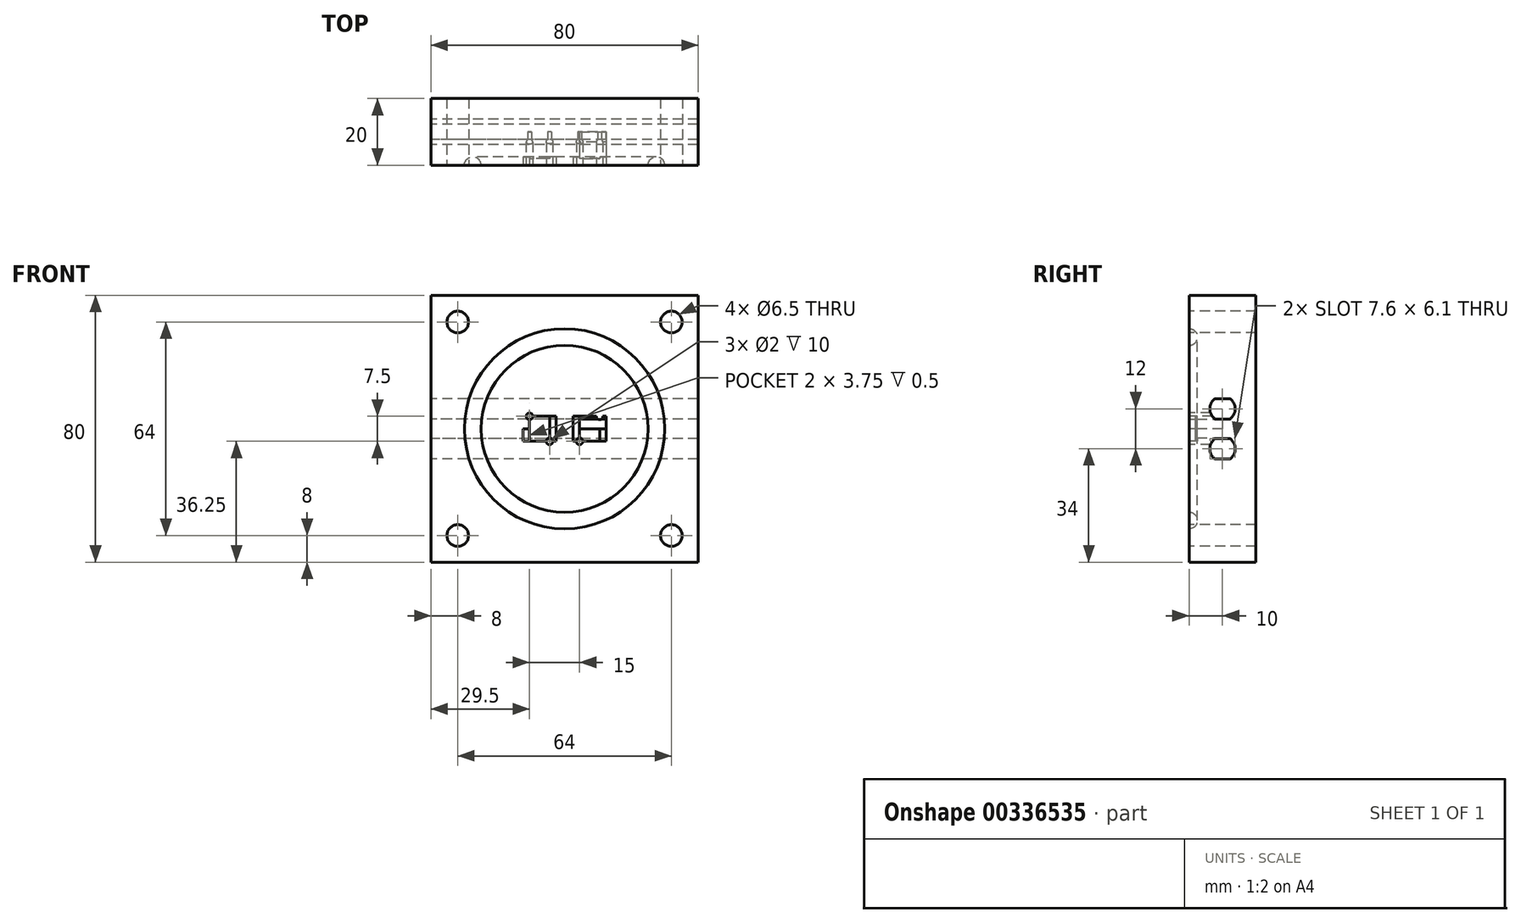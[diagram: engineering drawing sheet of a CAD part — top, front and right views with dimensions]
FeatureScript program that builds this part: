
annotation { "Feature Type Name" : "Feature", "Feature Type Description" : "" }
export const myFeature = defineFeature(function(context is Context, id is Id, definition is map)
    precondition{}
    {
        {
            assignVariable(context, id + "F0", {"name" : "Thickness", "anyValue" : 20});
        }
        {
            var Q0;
            Q0=qCreatedBy(makeId("Front.planeOp"),FACE);
            var sketch = newSketch(context, id + "F1", { "sketchPlane" : qUnion([Q0])});
            skLineSegment(sketch, "E0.bottom", {"start": v(0, 0) * mm, "end": v(80, 0) * mm});
            skLineSegment(sketch, "E0.top", {"start": v(0, 80) * mm, "end": v(80, 80) * mm});
            skLineSegment(sketch, "E0.left", {"start": v(0, 0) * mm, "end": v(0, 80) * mm});
            skLineSegment(sketch, "E0.right", {"start": v(80, 0) * mm, "end": v(80, 80) * mm});
            skSolve(sketch);
        }
        {
            var Q0;
            Q0=makeQuery(id+"F1.imprint","IMPRINT",FACE,{"disambiguationData":[TD([[makeQuery(id+"F1.imprint","IMPRINT",EDGE,{"derivedFrom":sQuery(id+"F1.wireOp",EDGE,"E0.bottom")}),1.0]])]});
            extrude(context, id + "F2", {"entities" : qUnion([Q0]), "depth" : (getVariable(context, 'Thickness')) * mm});
        }
        {
            assignVariable(context, id + "F3", {"name" : "G_thick", "anyValue" : 5});
        }
        {
            var Q0;
            Q0=makeQuery(id+"F2.opExtrude","CAP_FACE",FACE,{"disambiguationData":[OSD([sQuery(id+"F1.wireOp",EDGE,"E0.bottom"),sQuery(id+"F1.wireOp",EDGE,"E0.top"),sQuery(id+"F1.wireOp",EDGE,"E0.left"),sQuery(id+"F1.wireOp",EDGE,"E0.right")])],"isStart":false});
            var sketch = newSketch(context, id + "F4", { "sketchPlane" : qUnion([Q0])});
            skCircle(sketch, "E1", {"center": v(40, 40) * mm, "radius": 30 * mm});
            skCircle(sketch, "E2", {"center": v(40, 40) * mm, "radius": 25 * mm});
            skCircle(sketch, "E3", {"center": v(8, 72) * mm, "radius": 3.25 * mm});
            skCircle(sketch, "E4", {"center": v(8, 8) * mm, "radius": 3.25 * mm});
            skCircle(sketch, "E5", {"center": v(72, 8) * mm, "radius": 3.25 * mm});
            skCircle(sketch, "E6", {"center": v(72, 72) * mm, "radius": 3.25 * mm});
            skLineSegment(sketch, "E7.bottom", {"start": v(27.5, 45) * mm, "end": v(52.5, 45) * mm});
            skLineSegment(sketch, "E7.top", {"start": v(27.5, 35) * mm, "end": v(52.5, 35) * mm});
            skLineSegment(sketch, "E7.left", {"start": v(27.5, 45) * mm, "end": v(27.5, 35) * mm});
            skLineSegment(sketch, "E7.right", {"start": v(52.5, 45) * mm, "end": v(52.5, 35) * mm});
            skLineSegment(sketch, "E8", {"start": v(27.5, 40) * mm, "end": v(52.5, 40) * mm});
            skLineSegment(sketch, "E9.bottom", {"start": v(37.5, 36.25) * mm, "end": v(27.5, 36.25) * mm});
            skLineSegment(sketch, "E9.top", {"start": v(37.5, 43.75) * mm, "end": v(27.5, 43.75) * mm});
            skLineSegment(sketch, "E9.left", {"start": v(37.5, 36.25) * mm, "end": v(37.5, 43.75) * mm});
            skLineSegment(sketch, "E9.right", {"start": v(27.5, 36.25) * mm, "end": v(27.5, 43.75) * mm});
            skPoint(sketch, "E9.middle", {"position": v(32.5, 40) * mm});
            skLineSegment(sketch, "E10", {"start": v(40, 45) * mm, "end": v(40, 33.09) * mm});
            skPoint(sketch, "E10.endSnap0", {"position": v(40, 35) * mm});
            skLineSegment(sketch, "E11", {"start": v(40, 33.09) * mm, "end": v(40, 48.3) * mm, "construction": true});
            skLineSegment(sketch, "E12.MirrorCS", {"start": v(42.5, 43.75) * mm, "end": v(52.5, 43.75) * mm});
            skLineSegment(sketch, "E13.MirrorCS", {"start": v(42.5, 36.25) * mm, "end": v(42.5, 43.75) * mm});
            skLineSegment(sketch, "E14.MirrorCS", {"start": v(42.5, 36.25) * mm, "end": v(52.5, 36.25) * mm});
            skLineSegment(sketch, "E15.MirrorCS", {"start": v(52.5, 36.25) * mm, "end": v(52.5, 43.75) * mm});
            skLineSegment(sketch, "E16.bottom", {"start": v(37.5, 36.25) * mm, "end": v(35.5, 36.25) * mm});
            skLineSegment(sketch, "E16.top", {"start": v(37.5, 43.75) * mm, "end": v(35.5, 43.75) * mm});
            skLineSegment(sketch, "E16.right", {"start": v(35.5, 36.25) * mm, "end": v(35.5, 43.75) * mm});
            skLineSegment(sketch, "E17.bottom", {"start": v(27.5, 36.25) * mm, "end": v(29.5, 36.25) * mm});
            skLineSegment(sketch, "E17.top", {"start": v(27.5, 43.75) * mm, "end": v(29.5, 43.75) * mm});
            skLineSegment(sketch, "E17.right", {"start": v(29.5, 36.25) * mm, "end": v(29.5, 43.75) * mm});
            skLineSegment(sketch, "E18.MirrorCS", {"start": v(44.5, 36.25) * mm, "end": v(44.5, 43.75) * mm});
            skLineSegment(sketch, "E19.MirrorCS", {"start": v(42.5, 36.25) * mm, "end": v(44.5, 36.25) * mm});
            skLineSegment(sketch, "E20.MirrorCS", {"start": v(50.5, 36.25) * mm, "end": v(50.5, 43.75) * mm});
            skLineSegment(sketch, "E21.MirrorCS", {"start": v(52.5, 43.75) * mm, "end": v(50.5, 43.75) * mm});
            skCircle(sketch, "E22", {"center": v(29.5, 43.75) * mm, "radius": 1 * mm});
            skCircle(sketch, "E23", {"center": v(35.5, 36.25) * mm, "radius": 1 * mm});
            skCircle(sketch, "E24.MirrorC", {"center": v(44.5, 36.25) * mm, "radius": 1 * mm});
            skCircle(sketch, "E25.MirrorC", {"center": v(50.5, 43.75) * mm, "radius": 1 * mm});
            skSolve(sketch);
        }
        {
            var Q0;
            Q0=makeQuery(id+"F4.imprint","IMPRINT",FACE,{"disambiguationData":[TD([[makeQuery(id+"F4.imprint","IMPRINT",EDGE,{"derivedFrom":sQuery(id+"F4.wireOp",EDGE,"E5")}),1.0]])]});
            var Q1;
            Q1=makeQuery(id+"F4.imprint","IMPRINT",FACE,{"disambiguationData":[TD([[makeQuery(id+"F4.imprint","IMPRINT",EDGE,{"derivedFrom":sQuery(id+"F4.wireOp",EDGE,"E4")}),1.0]])]});
            var Q2;
            Q2=makeQuery(id+"F4.imprint","IMPRINT",FACE,{"disambiguationData":[TD([[makeQuery(id+"F4.imprint","IMPRINT",EDGE,{"derivedFrom":sQuery(id+"F4.wireOp",EDGE,"E3")}),1.0]])]});
            var Q3;
            Q3=makeQuery(id+"F4.imprint","IMPRINT",FACE,{"disambiguationData":[TD([[makeQuery(id+"F4.imprint","IMPRINT",EDGE,{"derivedFrom":sQuery(id+"F4.wireOp",EDGE,"E6")}),1.0]])]});
            var Q4;
            Q4=sQuery(id+"F4.wireOp",EDGE,"E3");
            extrude(context, id + "F5", {"entities" : qUnion([Q0, Q1, Q2, Q3]), "operationType" : NewBodyOperationType.REMOVE, "surfaceEntities" : qUnion([Q4]), "endBound" : BoundingType.THROUGH_ALL, "oppositeDirection" : true, "depth" : 25 * mm});
        }
        {
            var Q0;
            Q0=makeQuery(id+"F4.imprint","IMPRINT",FACE,{"disambiguationData":[TD([[makeQuery(id+"F4.imprint","IMPRINT",EDGE,{"derivedFrom":sQuery(id+"F4.wireOp",EDGE,"E1")}),1.0]])]});
            var Q1;
            Q1=sQuery(id+"F4.wireOp",EDGE,"E1");
            var Q2;
            Q2=sQuery(id+"F4.wireOp",EDGE,"E2");
            extrude(context, id + "F6", {"entities" : qUnion([Q0]), "operationType" : NewBodyOperationType.REMOVE, "surfaceEntities" : qUnion([Q1, Q2]), "oppositeDirection" : true, "depth" : 2.5 * mm});
        }
        {
            var Q0;
            Q0=makeQuery(id+"F6.boolean.opBoolean","COPY",EDGE,{"derivedFrom":makeQuery(id+"F6.opExtrude","CAP_EDGE",EDGE,{"disambiguationData":[OSD([sQuery(id+"F4.wireOp",EDGE,"E2")])],"isStart":false})});
            fillet(context, id + "F7", {"entities" : qUnion([Q0]), "radius" : (getVariable(context, 'G_thick') / 2) * mm, "tangentPropagation" : true, "allowEdgeOverflow" : false});
        }
        {
            var Q0;
            Q0=makeQuery(id+"F6.boolean.opBoolean","COPY",EDGE,{"derivedFrom":makeQuery(id+"F6.opExtrude","CAP_EDGE",EDGE,{"disambiguationData":[OSD([sQuery(id+"F4.wireOp",EDGE,"E1")])],"isStart":false})});
            fillet(context, id + "F8", {"entities" : qUnion([Q0]), "radius" : (getVariable(context, 'G_thick') / 2) * mm, "tangentPropagation" : true, "allowEdgeOverflow" : false});
        }
        {
            var Q0;
            {var subQ5=sQuery(id+"F4.wireOp",EDGE,"E17.top");Q0=makeQuery(id+"F4.imprint","IMPRINT",FACE,{"disambiguationData":[TD([[makeQuery(id+"F4.imprint","IMPRINT",EDGE,{"derivedFrom":subQ5}),-1.0]])]});}
            var Q1;
            {var subQ5=sQuery(id+"F4.wireOp",EDGE,"E17.bottom");Q1=makeQuery(id+"F4.imprint","IMPRINT",FACE,{"disambiguationData":[TD([[makeQuery(id+"F4.imprint","IMPRINT",EDGE,{"derivedFrom":subQ5}),1.0]])]});}
            var Q2;
            {var subQ5=sQuery(id+"F4.wireOp",EDGE,"E16.top");Q2=makeQuery(id+"F4.imprint","IMPRINT",FACE,{"disambiguationData":[TD([[makeQuery(id+"F4.imprint","IMPRINT",EDGE,{"derivedFrom":subQ5}),1.0]])]});}
            var Q3;
            {var subQ5=sQuery(id+"F4.wireOp",EDGE,"E16.bottom");Q3=makeQuery(id+"F4.imprint","IMPRINT",FACE,{"disambiguationData":[TD([[makeQuery(id+"F4.imprint","IMPRINT",EDGE,{"derivedFrom":subQ5}),-1.0]])]});}
            var Q4;
            {var subQ0=sQuery(id+"F4.wireOp",EDGE,"E13.MirrorCS");var subQ1=sQuery(id+"F4.wireOp",EDGE,"E8");var subQ2=makeQuery(id+"F4.imprint","INTERSECT",VERTEX,{"derivedFrom":[subQ1,subQ0]});Q4=makeQuery(id+"F4.imprint","IMPRINT",FACE,{"disambiguationData":[TD([[makeQuery(id+"F4.imprint","IMPRINT",EDGE,{"disambiguationData":[TD([[subQ2,-1.0]])],"derivedFrom":subQ1}),1.0]])]});}
            var Q5;
            {var subQ0=sQuery(id+"F4.wireOp",EDGE,"E13.MirrorCS");var subQ1=sQuery(id+"F4.wireOp",EDGE,"E8");var subQ2=makeQuery(id+"F4.imprint","INTERSECT",VERTEX,{"derivedFrom":[subQ1,subQ0]});Q5=makeQuery(id+"F4.imprint","IMPRINT",FACE,{"disambiguationData":[TD([[makeQuery(id+"F4.imprint","IMPRINT",EDGE,{"disambiguationData":[TD([[subQ2,-1.0]])],"derivedFrom":subQ1}),-1.0]])]});}
            var Q6;
            {var subQ0=sQuery(id+"F4.wireOp",EDGE,"E15.MirrorCS");var subQ1=sQuery(id+"F4.wireOp",EDGE,"E8");var subQ2=makeQuery(id+"F4.imprint","INTERSECT",VERTEX,{"derivedFrom":[subQ1,subQ0]});Q6=makeQuery(id+"F4.imprint","IMPRINT",FACE,{"disambiguationData":[TD([[makeQuery(id+"F4.imprint","IMPRINT",EDGE,{"disambiguationData":[TD([[subQ2,1.0]])],"derivedFrom":subQ1}),-1.0]])]});}
            var Q7;
            {var subQ5=sQuery(id+"F4.wireOp",EDGE,"E21.MirrorCS");Q7=makeQuery(id+"F4.imprint","IMPRINT",FACE,{"disambiguationData":[TD([[makeQuery(id+"F4.imprint","IMPRINT",EDGE,{"derivedFrom":subQ5}),1.0]])]});}
            var Q8;
            {var subQ0=sQuery(id+"F4.wireOp",EDGE,"E9.right");var subQ1=sQuery(id+"F4.wireOp",EDGE,"E8");var subQ2=makeQuery(id+"F4.imprint","INTERSECT",VERTEX,{"derivedFrom":[subQ1,subQ0]});Q8=makeQuery(id+"F4.imprint","IMPRINT",FACE,{"disambiguationData":[TD([[makeQuery(id+"F4.imprint","IMPRINT",EDGE,{"disambiguationData":[TD([[subQ2,-1.0]])],"derivedFrom":subQ1}),1.0]])]});}
            var Q9;
            {var subQ0=sQuery(id+"F4.wireOp",EDGE,"E16.right");var subQ1=sQuery(id+"F4.wireOp",EDGE,"E8");var subQ2=makeQuery(id+"F4.imprint","INTERSECT",VERTEX,{"derivedFrom":[subQ1,subQ0]});Q9=makeQuery(id+"F4.imprint","IMPRINT",FACE,{"disambiguationData":[TD([[makeQuery(id+"F4.imprint","IMPRINT",EDGE,{"disambiguationData":[TD([[subQ2,-1.0]])],"derivedFrom":subQ1}),-1.0]])]});}
            var Q10;
            {var subQ0=sQuery(id+"F4.wireOp",EDGE,"E15.MirrorCS");var subQ5=sQuery(id+"F4.wireOp",EDGE,"E8");var subQ6=makeQuery(id+"F4.imprint","INTERSECT",VERTEX,{"derivedFrom":[subQ5,subQ0]});Q10=makeQuery(id+"F4.imprint","IMPRINT",FACE,{"disambiguationData":[TD([[makeQuery(id+"F4.imprint","IMPRINT",EDGE,{"disambiguationData":[TD([[subQ6,1.0]])],"derivedFrom":subQ5}),1.0]])]});}
            var Q11;
            {var subQ0=sQuery(id+"F4.wireOp",EDGE,"E14.MirrorCS");var subQ1=sQuery(id+"F4.wireOp",EDGE,"E18.MirrorCS");var subQ2=makeQuery(id+"F4.imprint","INTERSECT",VERTEX,{"derivedFrom":[subQ1,subQ0]});Q11=makeQuery(id+"F4.imprint","IMPRINT",FACE,{"disambiguationData":[TD([[makeQuery(id+"F4.imprint","IMPRINT",EDGE,{"disambiguationData":[TD([[subQ2,-1.0]])],"derivedFrom":subQ1}),1.0]])]});}
            var Q12;
            Q12=sQuery(id+"F4.wireOp",EDGE,"E9.bottom");
            extrude(context, id + "F9", {"entities" : qUnion([Q0, Q1, Q2, Q3, Q4, Q5, Q6, Q7, Q8, Q9, Q10, Q11]), "operationType" : NewBodyOperationType.REMOVE, "surfaceEntities" : qUnion([Q12]), "oppositeDirection" : true, "depth" : 2.5 * mm});
        }
        {
            var Q0;
            {var subQ1=sQuery(id+"F4.wireOp",EDGE,"E9.top");var subQ3=sQuery(id+"F4.wireOp",EDGE,"E22");var subQ4=makeQuery(id+"F4.imprint","INTERSECT",VERTEX,{"derivedFrom":[subQ1,subQ3]});Q0=makeQuery(id+"F4.imprint","IMPRINT",FACE,{"disambiguationData":[TD([[makeQuery(id+"F4.imprint","IMPRINT",EDGE,{"disambiguationData":[TD([[subQ4,-1.0]])],"derivedFrom":subQ3}),1.0]])]});}
            var Q1;
            {var subQ1=sQuery(id+"F4.wireOp",EDGE,"E17.top");var subQ3=sQuery(id+"F4.wireOp",EDGE,"E22");var subQ4=makeQuery(id+"F4.imprint","INTERSECT",VERTEX,{"derivedFrom":[subQ1,subQ3]});Q1=makeQuery(id+"F4.imprint","IMPRINT",FACE,{"disambiguationData":[TD([[makeQuery(id+"F4.imprint","IMPRINT",EDGE,{"disambiguationData":[TD([[subQ4,-1.0]])],"derivedFrom":subQ3}),1.0]])]});}
            var Q2;
            {var subQ1=sQuery(id+"F4.wireOp",EDGE,"E9.top");var subQ3=sQuery(id+"F4.wireOp",EDGE,"E22");var subQ4=makeQuery(id+"F4.imprint","INTERSECT",VERTEX,{"derivedFrom":[subQ1,subQ3]});Q2=makeQuery(id+"F4.imprint","IMPRINT",FACE,{"disambiguationData":[TD([[makeQuery(id+"F4.imprint","IMPRINT",EDGE,{"disambiguationData":[TD([[subQ4,1.0]])],"derivedFrom":subQ3}),1.0]])]});}
            var Q3;
            {var subQ1=sQuery(id+"F4.wireOp",EDGE,"E9.bottom");var subQ3=sQuery(id+"F4.wireOp",EDGE,"E23");var subQ4=makeQuery(id+"F4.imprint","INTERSECT",VERTEX,{"derivedFrom":[subQ1,subQ3]});Q3=makeQuery(id+"F4.imprint","IMPRINT",FACE,{"disambiguationData":[TD([[makeQuery(id+"F4.imprint","IMPRINT",EDGE,{"disambiguationData":[TD([[subQ4,1.0]])],"derivedFrom":subQ3}),1.0]])]});}
            var Q4;
            {var subQ1=sQuery(id+"F4.wireOp",EDGE,"E16.bottom");var subQ3=sQuery(id+"F4.wireOp",EDGE,"E23");var subQ4=makeQuery(id+"F4.imprint","INTERSECT",VERTEX,{"derivedFrom":[subQ1,subQ3]});Q4=makeQuery(id+"F4.imprint","IMPRINT",FACE,{"disambiguationData":[TD([[makeQuery(id+"F4.imprint","IMPRINT",EDGE,{"disambiguationData":[TD([[subQ4,-1.0]])],"derivedFrom":subQ3}),1.0]])]});}
            var Q5;
            {var subQ1=sQuery(id+"F4.wireOp",EDGE,"E9.bottom");var subQ3=sQuery(id+"F4.wireOp",EDGE,"E23");var subQ4=makeQuery(id+"F4.imprint","INTERSECT",VERTEX,{"derivedFrom":[subQ1,subQ3]});Q5=makeQuery(id+"F4.imprint","IMPRINT",FACE,{"disambiguationData":[TD([[makeQuery(id+"F4.imprint","IMPRINT",EDGE,{"disambiguationData":[TD([[subQ4,-1.0]])],"derivedFrom":subQ3}),1.0]])]});}
            var Q6;
            {var subQ0=sQuery(id+"F4.wireOp",EDGE,"E14.MirrorCS");var subQ1=sQuery(id+"F4.wireOp",EDGE,"E18.MirrorCS");var subQ2=makeQuery(id+"F4.imprint","INTERSECT",VERTEX,{"derivedFrom":[subQ1,subQ0]});Q6=makeQuery(id+"F4.imprint","IMPRINT",FACE,{"disambiguationData":[TD([[makeQuery(id+"F4.imprint","IMPRINT",EDGE,{"disambiguationData":[TD([[subQ2,-1.0]])],"derivedFrom":subQ1}),1.0]])]});}
            var Q7;
            {var subQ0=sQuery(id+"F4.wireOp",EDGE,"E14.MirrorCS");var subQ1=sQuery(id+"F4.wireOp",EDGE,"E18.MirrorCS");var subQ2=makeQuery(id+"F4.imprint","INTERSECT",VERTEX,{"derivedFrom":[subQ1,subQ0]});Q7=makeQuery(id+"F4.imprint","IMPRINT",FACE,{"disambiguationData":[TD([[makeQuery(id+"F4.imprint","IMPRINT",EDGE,{"disambiguationData":[TD([[subQ2,-1.0]])],"derivedFrom":subQ1}),-1.0]])]});}
            var Q8;
            {var subQ0=sQuery(id+"F4.wireOp",EDGE,"E14.MirrorCS");var subQ1=makeQuery(id+"F4.imprint","INTERSECT",VERTEX,{"derivedFrom":[sQuery(id+"F4.wireOp",EDGE,"E18.MirrorCS"),subQ0]});Q8=makeQuery(id+"F4.imprint","IMPRINT",FACE,{"disambiguationData":[TD([[makeQuery(id+"F4.imprint","IMPRINT",EDGE,{"disambiguationData":[TD([[subQ1,1.0]])],"derivedFrom":subQ0}),-1.0]])]});}
            var Q9;
            {var subQ1=sQuery(id+"F4.wireOp",EDGE,"E12.MirrorCS");var subQ3=sQuery(id+"F4.wireOp",EDGE,"E25.MirrorC");var subQ4=makeQuery(id+"F4.imprint","INTERSECT",VERTEX,{"derivedFrom":[subQ1,subQ3]});Q9=makeQuery(id+"F4.imprint","IMPRINT",FACE,{"disambiguationData":[TD([[makeQuery(id+"F4.imprint","IMPRINT",EDGE,{"disambiguationData":[TD([[subQ4,-1.0]])],"derivedFrom":subQ3}),-1.0]])]});}
            var Q10;
            {var subQ1=sQuery(id+"F4.wireOp",EDGE,"E12.MirrorCS");var subQ3=sQuery(id+"F4.wireOp",EDGE,"E25.MirrorC");var subQ4=makeQuery(id+"F4.imprint","INTERSECT",VERTEX,{"derivedFrom":[subQ1,subQ3]});Q10=makeQuery(id+"F4.imprint","IMPRINT",FACE,{"disambiguationData":[TD([[makeQuery(id+"F4.imprint","IMPRINT",EDGE,{"disambiguationData":[TD([[subQ4,1.0]])],"derivedFrom":subQ3}),-1.0]])]});}
            var Q11;
            {var subQ1=sQuery(id+"F4.wireOp",EDGE,"E20.MirrorCS");var subQ3=sQuery(id+"F4.wireOp",EDGE,"E25.MirrorC");var subQ4=makeQuery(id+"F4.imprint","INTERSECT",VERTEX,{"derivedFrom":[subQ1,subQ3]});Q11=makeQuery(id+"F4.imprint","IMPRINT",FACE,{"disambiguationData":[TD([[makeQuery(id+"F4.imprint","IMPRINT",EDGE,{"disambiguationData":[TD([[subQ4,1.0]])],"derivedFrom":subQ3}),-1.0]])]});}
            extrude(context, id + "F10", {"entities" : qUnion([Q0, Q1, Q2, Q3, Q4, Q5, Q6, Q7, Q8, Q9, Q10, Q11]), "operationType" : NewBodyOperationType.REMOVE, "oppositeDirection" : true, "depth" : 10 * mm});
        }
        {
            var Q0;
            Q0=makeQuery(id+"F2.opExtrude","SWEPT_FACE",FACE,{"disambiguationData":[OSD([sQuery(id+"F1.wireOp",EDGE,"E0.left")])]});
            var sketch = newSketch(context, id + "F11", { "sketchPlane" : qUnion([Q0])});
            skCircle(sketch, "E26", {"center": v(10, 46) * mm, "radius": 3.8 * mm});
            skLineSegment(sketch, "E27", {"start": v(10, 80) * mm, "end": v(10, 0) * mm, "construction": true});
            skLineSegment(sketch, "E28", {"start": v(0, 40) * mm, "end": v(20.23, 40) * mm, "construction": true});
            skPoint(sketch, "E28.endSnap0", {"position": v(20, 40) * mm});
            skLineSegment(sketch, "E29", {"start": v(12.27, 42.95) * mm, "end": v(7.73, 42.95) * mm});
            skLineSegment(sketch, "E30", {"start": v(12.27, 49.05) * mm, "end": v(7.73, 49.05) * mm});
            skCircle(sketch, "E31.MirrorC", {"center": v(10, 34) * mm, "radius": 3.8 * mm});
            skLineSegment(sketch, "E32.MirrorCS", {"start": v(12.27, 30.95) * mm, "end": v(7.73, 30.95) * mm});
            skLineSegment(sketch, "E33.MirrorCS", {"start": v(12.27, 37.05) * mm, "end": v(7.73, 37.05) * mm});
            skSolve(sketch);
        }
        {
            var Q0;
            Q0=makeQuery(id+"F11.imprint","IMPRINT",FACE,{"disambiguationData":[TD([[makeQuery(id+"F11.imprint","IMPRINT",EDGE,{"derivedFrom":sQuery(id+"F11.wireOp",EDGE,"E26")}),1.0]])]});
            extrude(context, id + "F12", {"entities" : qUnion([Q0]), "operationType" : NewBodyOperationType.REMOVE, "endBound" : BoundingType.THROUGH_ALL, "oppositeDirection" : true, "depth" : 25 * mm});
        }
        {
            var Q0;
            {var subQ0=sQuery(id+"F11.wireOp",EDGE,"E29");Q0=makeQuery(id+"F11.imprint","IMPRINT",FACE,{"disambiguationData":[TD([[makeQuery(id+"F11.imprint","IMPRINT",EDGE,{"derivedFrom":subQ0}),-1.0]])]});}
            var Q1;
            {var subQ0=sQuery(id+"F11.wireOp",EDGE,"E32.MirrorCS");Q1=makeQuery(id+"F11.imprint","IMPRINT",FACE,{"disambiguationData":[TD([[makeQuery(id+"F11.imprint","IMPRINT",EDGE,{"derivedFrom":subQ0}),-1.0]])]});}
            extrude(context, id + "F13", {"entities" : qUnion([Q0, Q1]), "operationType" : NewBodyOperationType.REMOVE, "endBound" : BoundingType.THROUGH_ALL, "oppositeDirection" : true, "depth" : 25 * mm});
        }
        {
            var Q0;
            {var subQ0=sQuery(id+"F4.wireOp",EDGE,"E17.right");var subQ1=sQuery(id+"F4.wireOp",EDGE,"E8");var subQ2=makeQuery(id+"F4.imprint","INTERSECT",VERTEX,{"derivedFrom":[subQ1,subQ0]});Q0=makeQuery(id+"F4.imprint","IMPRINT",FACE,{"disambiguationData":[TD([[makeQuery(id+"F4.imprint","IMPRINT",EDGE,{"disambiguationData":[TD([[subQ2,-1.0]])],"derivedFrom":subQ1}),1.0]])]});}
            var Q1;
            {var subQ0=sQuery(id+"F4.wireOp",EDGE,"E17.right");var subQ3=sQuery(id+"F4.wireOp",EDGE,"E8");var subQ4=makeQuery(id+"F4.imprint","INTERSECT",VERTEX,{"derivedFrom":[subQ3,subQ0]});Q1=makeQuery(id+"F4.imprint","IMPRINT",FACE,{"disambiguationData":[TD([[makeQuery(id+"F4.imprint","IMPRINT",EDGE,{"disambiguationData":[TD([[subQ4,-1.0]])],"derivedFrom":subQ3}),-1.0]])]});}
            var Q2;
            {var subQ1=sQuery(id+"F4.wireOp",EDGE,"E8");var subQ6=sQuery(id+"F4.wireOp",EDGE,"E18.MirrorCS");var subQ8=makeQuery(id+"F4.imprint","INTERSECT",VERTEX,{"derivedFrom":[subQ1,subQ6]});Q2=makeQuery(id+"F4.imprint","IMPRINT",FACE,{"disambiguationData":[TD([[makeQuery(id+"F4.imprint","IMPRINT",EDGE,{"disambiguationData":[TD([[subQ8,-1.0]])],"derivedFrom":subQ1}),1.0]])]});}
            var Q3;
            {var subQ3=sQuery(id+"F4.wireOp",EDGE,"E8");var subQ7=sQuery(id+"F4.wireOp",EDGE,"E18.MirrorCS");var subQ8=makeQuery(id+"F4.imprint","INTERSECT",VERTEX,{"derivedFrom":[subQ3,subQ7]});Q3=makeQuery(id+"F4.imprint","IMPRINT",FACE,{"disambiguationData":[TD([[makeQuery(id+"F4.imprint","IMPRINT",EDGE,{"disambiguationData":[TD([[subQ8,-1.0]])],"derivedFrom":subQ3}),-1.0]])]});}
            extrude(context, id + "F14", {"entities" : qUnion([Q0, Q1, Q2, Q3]), "operationType" : NewBodyOperationType.REMOVE, "oppositeDirection" : true, "depth" : 2 * mm});
        }
    });
